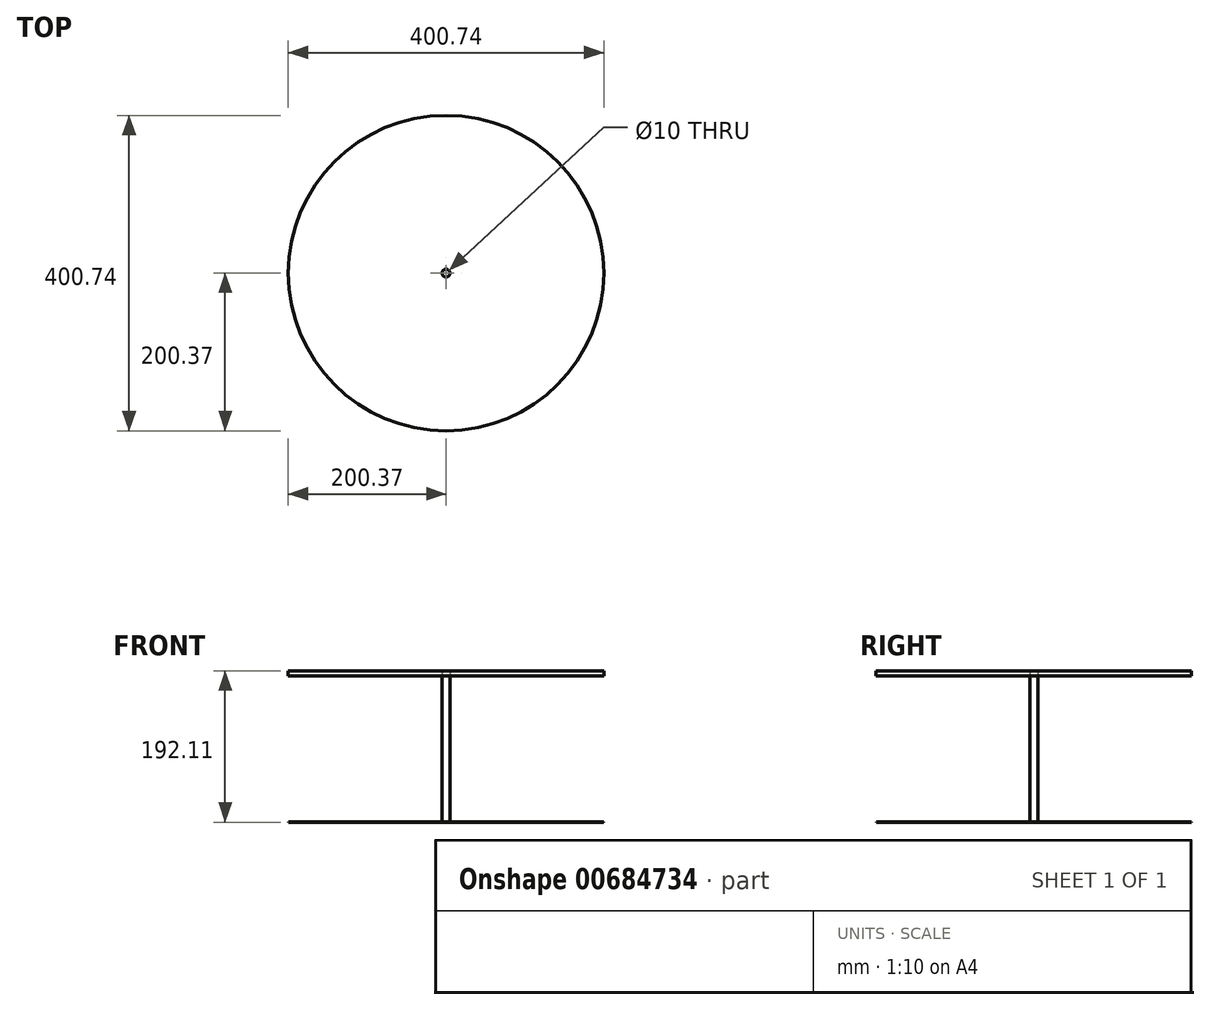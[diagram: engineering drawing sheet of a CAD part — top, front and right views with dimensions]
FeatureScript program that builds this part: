
annotation { "Feature Type Name" : "Feature", "Feature Type Description" : "" }
export const myFeature = defineFeature(function(context is Context, id is Id, definition is map)
    precondition{}
    {
        {
            var Q0;
            Q0=qCreatedBy(makeId("Top.planeOp"),FACE);
            var sketch = newSketch(context, id + "F0", { "sketchPlane" : qUnion([Q0])});
            skCircle(sketch, "E0", {"center": v(0, 0) * mm, "radius": 200 * mm});
            skSolve(sketch);
        }
        {
            var Q0;
            Q0 = qSketchRegion(id + "F0", true);
            extrude(context, id + "F1", {"entities" : qUnion([Q0]), "depth" : 1 / 101.6 * mm, "offsetDistance" : 25.4 * mm});
        }
        {
            var Q0;
            Q0=makeQuery(id+"F1.opExtrude","CAP_FACE",FACE,{"disambiguationData":[OSD([sQuery(id+"F0.wireOp",EDGE,"E0")])],"isStart":false});
            var sketch = newSketch(context, id + "F2", { "sketchPlane" : qUnion([Q0])});
            skCircle(sketch, "E1", {"center": v(0, 0) * mm, "radius": 5 * mm});
            skSolve(sketch);
        }
        {
            var Q0;
            Q0 = qSketchRegion(id + "F2", true);
            extrude(context, id + "F3", {"entities" : qUnion([Q0]), "operationType" : NewBodyOperationType.ADD, "depth" : 185.75 * mm, "offsetDistance" : 25.4 * mm});
        }
        {
            var Q0;
            Q0=makeQuery(id+"F3.opExtrude","CAP_FACE",FACE,{"disambiguationData":[OSD([sQuery(id+"F2.wireOp",EDGE,"E1")])],"isStart":false});
            var sketch = newSketch(context, id + "F4", { "sketchPlane" : qUnion([Q0])});
            skCircle(sketch, "E2", {"center": v(0, 0) * mm, "radius": 200.37 * mm});
            skSolve(sketch);
        }
        {
            var Q0;
            Q0=makeQuery(id+"F4.imprint","IMPRINT",FACE,{"disambiguationData":[TD([[makeQuery(id+"F4.imprint","IMPRINT",EDGE,{"derivedFrom":sQuery(id+"F4.wireOp",EDGE,"E2")}),1.0]])]});
            extrude(context, id + "F5", {"entities" : qUnion([Q0]), "depth" : 6.35 * mm, "offsetDistance" : 25.4 * mm});
        }
    });
